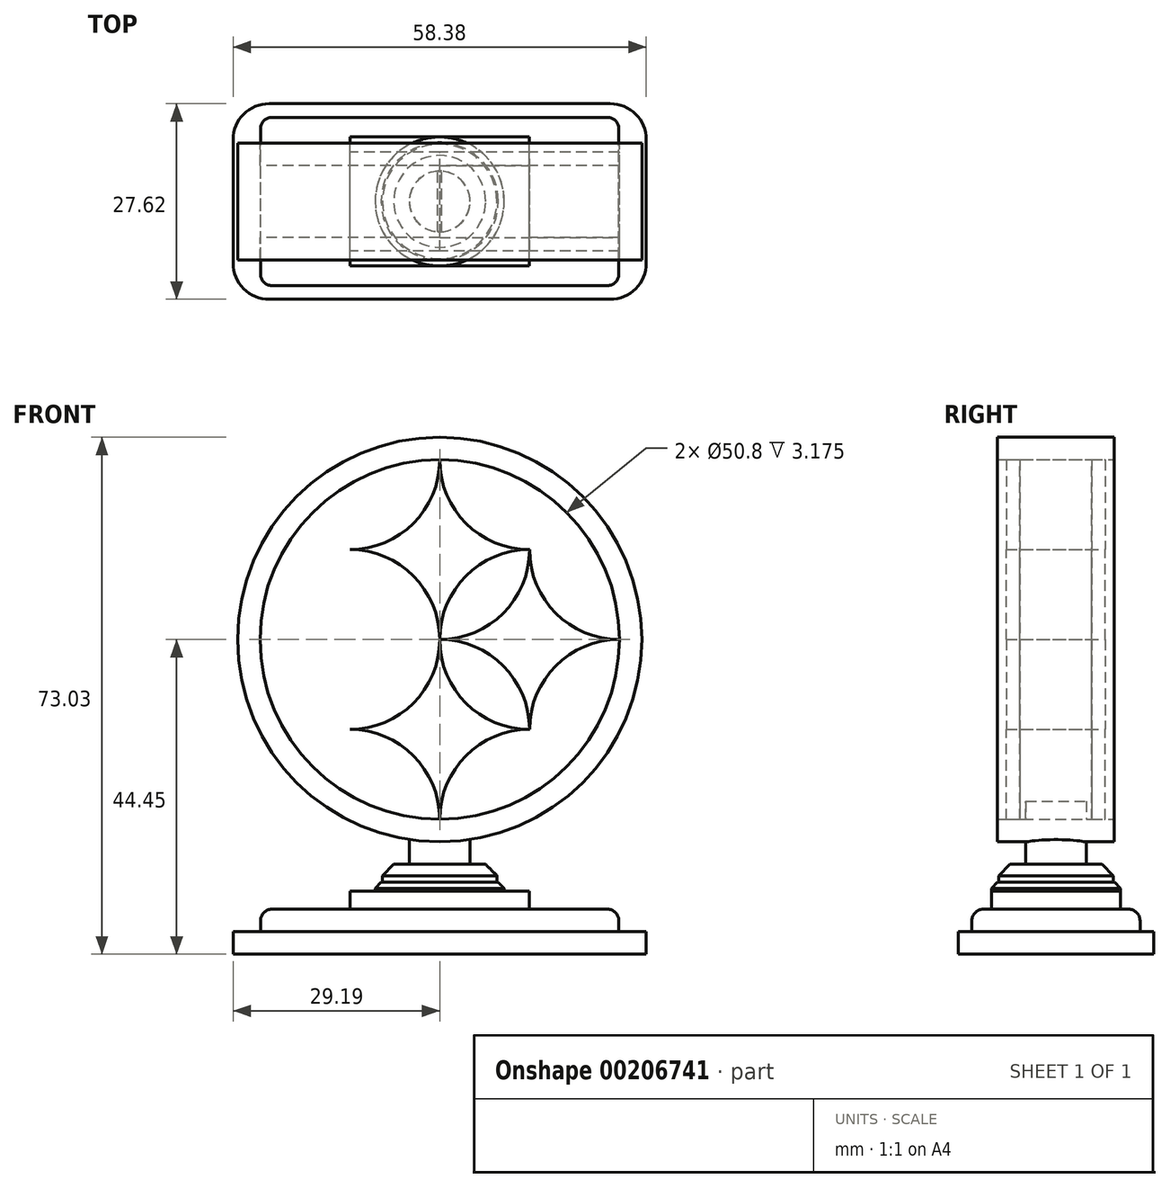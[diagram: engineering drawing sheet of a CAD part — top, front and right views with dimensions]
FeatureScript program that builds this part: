
annotation { "Feature Type Name" : "Feature", "Feature Type Description" : "" }
export const myFeature = defineFeature(function(context is Context, id is Id, definition is map)
    precondition{}
    {
        {
            var Q0;
            Q0=qCreatedBy(makeId("Front.planeOp"),FACE);
            var sketch = newSketch(context, id + "F0", { "sketchPlane" : qUnion([Q0])});
            skCircle(sketch, "E0", {"center": v(0, 44.45) * mm, "radius": 25.4 * mm});
            skCircle(sketch, "E1", {"center": v(0, 44.45) * mm, "radius": 28.58 * mm});
            skArc(sketch, "E2", {"start": v(-12.7, 31.75) * mm, "mid": v(0, 44.45) * mm, "end": v(-12.7, 57.15) * mm});
            skArc(sketch, "E3", {"start": v(12.7, 31.75) * mm, "mid": v(8.98, 40.73) * mm, "end": v(0, 44.45) * mm});
            skArc(sketch, "E4", {"start": v(0, 44.45) * mm, "mid": v(8.98, 48.17) * mm, "end": v(12.7, 57.15) * mm});
            skArc(sketch, "E5", {"start": v(12.7, 57.15) * mm, "mid": v(0, 44.45) * mm, "end": v(12.7, 31.75) * mm});
            skArc(sketch, "E6", {"start": v(0, 69.85) * mm, "mid": v(3.72, 60.87) * mm, "end": v(12.7, 57.15) * mm});
            skArc(sketch, "E7", {"start": v(12.7, 57.15) * mm, "mid": v(16.42, 48.17) * mm, "end": v(25.4, 44.45) * mm});
            skArc(sketch, "E8", {"start": v(25.4, 44.45) * mm, "mid": v(16.42, 40.73) * mm, "end": v(12.7, 31.75) * mm});
            skArc(sketch, "E9.trimOffspring", {"start": v(-12.7, 57.15) * mm, "mid": v(-3.72, 60.87) * mm, "end": v(0, 69.85) * mm});
            skArc(sketch, "E10.trimOffspring", {"start": v(0, 19.05) * mm, "mid": v(-3.72, 28.03) * mm, "end": v(-12.7, 31.75) * mm});
            skArc(sketch, "E11.trimOffspring", {"start": v(12.7, 31.75) * mm, "mid": v(3.72, 28.03) * mm, "end": v(0, 19.05) * mm});
            skSolve(sketch);
        }
        {
            var Q0;
            Q0=qCreatedBy(makeId("Top.planeOp"),FACE);
            var sketch = newSketch(context, id + "F1", { "sketchPlane" : qUnion([Q0])});
            skLineSegment(sketch, "E12.bottom", {"start": v(29.2, -13.81) * mm, "end": v(-29.2, -13.81) * mm});
            skLineSegment(sketch, "E12.top", {"start": v(29.2, 13.81) * mm, "end": v(-29.2, 13.81) * mm});
            skLineSegment(sketch, "E12.left", {"start": v(29.2, -13.81) * mm, "end": v(29.2, 13.81) * mm});
            skLineSegment(sketch, "E12.right", {"start": v(-29.2, -13.81) * mm, "end": v(-29.2, 13.81) * mm});
            skPoint(sketch, "E12.middle", {"position": v(0, 0) * mm});
            skLineSegment(sketch, "E13.bottom", {"start": v(25.33, -11.88) * mm, "end": v(-25.33, -11.88) * mm});
            skLineSegment(sketch, "E13.top", {"start": v(25.33, 11.88) * mm, "end": v(-25.33, 11.88) * mm});
            skLineSegment(sketch, "E13.left", {"start": v(25.33, -11.88) * mm, "end": v(25.33, 11.88) * mm});
            skLineSegment(sketch, "E13.right", {"start": v(-25.33, -11.88) * mm, "end": v(-25.33, 11.88) * mm});
            skLineSegment(sketch, "E14.bottom", {"start": v(12.66, -9.11) * mm, "end": v(-12.66, -9.11) * mm});
            skLineSegment(sketch, "E14.top", {"start": v(12.66, 9.11) * mm, "end": v(-12.66, 9.11) * mm});
            skLineSegment(sketch, "E14.left", {"start": v(12.66, -9.11) * mm, "end": v(12.66, 9.11) * mm});
            skLineSegment(sketch, "E14.right", {"start": v(-12.66, -9.11) * mm, "end": v(-12.66, 9.11) * mm});
            skCircle(sketch, "E15", {"center": v(0, 0) * mm, "radius": 9.11 * mm});
            skCircle(sketch, "E16", {"center": v(0, 0) * mm, "radius": 8.1 * mm});
            skCircle(sketch, "E17", {"center": v(0, 0) * mm, "radius": 4.29 * mm});
            skSolve(sketch);
        }
        {
            var Q0;
            Q0=makeQuery(id+"F1.imprint","IMPRINT",FACE,{"disambiguationData":[TD([[makeQuery(id+"F1.imprint","IMPRINT",EDGE,{"derivedFrom":sQuery(id+"F1.wireOp",EDGE,"E17")}),1.0]])]});
            extrude(context, id + "F2", {"entities" : qUnion([Q0]), "depth" : 21.59 * mm});
        }
        {
            var Q0;
            Q0=makeQuery(id+"F1.imprint","IMPRINT",FACE,{"disambiguationData":[TD([[makeQuery(id+"F1.imprint","IMPRINT",EDGE,{"derivedFrom":sQuery(id+"F1.wireOp",EDGE,"E16")}),1.0]])]});
            extrude(context, id + "F3", {"entities" : qUnion([Q0]), "operationType" : NewBodyOperationType.ADD, "depth" : 12.7 * mm});
        }
        {
            var Q0;
            Q0=makeQuery(id+"F1.imprint","IMPRINT",FACE,{"disambiguationData":[TD([[makeQuery(id+"F1.imprint","IMPRINT",EDGE,{"derivedFrom":sQuery(id+"F1.wireOp",EDGE,"E16")}),-1.0]])]});
            extrude(context, id + "F4", {"entities" : qUnion([Q0]), "operationType" : NewBodyOperationType.ADD, "depth" : 10.16 * mm});
        }
        {
            var Q0;
            {var subQ0=sQuery(id+"F1.wireOp",EDGE,"E14.right");Q0=makeQuery(id+"F1.imprint","IMPRINT",FACE,{"disambiguationData":[TD([[makeQuery(id+"F1.imprint","IMPRINT",EDGE,{"derivedFrom":subQ0}),-1.0]])]});}
            var Q1;
            {var subQ0=sQuery(id+"F1.wireOp",EDGE,"E14.left");Q1=makeQuery(id+"F1.imprint","IMPRINT",FACE,{"disambiguationData":[TD([[makeQuery(id+"F1.imprint","IMPRINT",EDGE,{"derivedFrom":subQ0}),1.0]])]});}
            extrude(context, id + "F5", {"entities" : qUnion([Q0, Q1]), "operationType" : NewBodyOperationType.ADD, "depth" : 8.9 * mm});
        }
        {
            var Q0;
            Q0=makeQuery(id+"F1.imprint","IMPRINT",FACE,{"disambiguationData":[TD([[makeQuery(id+"F1.imprint","IMPRINT",EDGE,{"derivedFrom":sQuery(id+"F1.wireOp",EDGE,"E13.bottom")}),-1.0]])]});
            extrude(context, id + "F6", {"entities" : qUnion([Q0]), "operationType" : NewBodyOperationType.ADD, "depth" : 6.35 * mm});
        }
        {
            var Q0;
            Q0=makeQuery(id+"F1.imprint","IMPRINT",FACE,{"disambiguationData":[TD([[makeQuery(id+"F1.imprint","IMPRINT",EDGE,{"derivedFrom":sQuery(id+"F1.wireOp",EDGE,"E12.bottom")}),-1.0]])]});
            extrude(context, id + "F7", {"entities" : qUnion([Q0]), "operationType" : NewBodyOperationType.ADD, "depth" : 3.17 * mm});
        }
        {
            var Q0;
            Q0=makeQuery(id+"F6.opExtrude","CAP_EDGE",EDGE,{"disambiguationData":[OSD([sQuery(id+"F1.wireOp",EDGE,"E13.bottom")])],"isStart":false});
            fillet(context, id + "F8", {"entities" : qUnion([Q0]), "radius" : 1.6 * mm, "tangentPropagation" : true, "allowEdgeOverflow" : false});
        }
        {
            var Q0;
            Q0=makeQuery(id+"F6.opExtrude","CAP_EDGE",EDGE,{"disambiguationData":[OSD([sQuery(id+"F1.wireOp",EDGE,"E13.right")])],"isStart":false});
            fillet(context, id + "F9", {"entities" : qUnion([Q0]), "radius" : 1.6 * mm, "tangentPropagation" : true, "allowEdgeOverflow" : false});
        }
        {
            var Q0;
            Q0=makeQuery(id+"F6.opExtrude","CAP_EDGE",EDGE,{"disambiguationData":[OSD([sQuery(id+"F1.wireOp",EDGE,"E13.left")])],"isStart":false});
            fillet(context, id + "F10", {"entities" : qUnion([Q0]), "radius" : 1.6 * mm, "tangentPropagation" : true, "allowEdgeOverflow" : false});
        }
        {
            var Q0;
            Q0=makeQuery(id+"F6.opExtrude","CAP_EDGE",EDGE,{"disambiguationData":[OSD([sQuery(id+"F1.wireOp",EDGE,"E13.top")])],"isStart":false});
            fillet(context, id + "F11", {"entities" : qUnion([Q0]), "radius" : 1.6 * mm, "tangentPropagation" : true, "allowEdgeOverflow" : false});
        }
        {
            var Q0;
            Q0=makeQuery(id+"F4.opExtrude","CAP_EDGE",EDGE,{"disambiguationData":[OSD([sQuery(id+"F1.wireOp",EDGE,"E15")])],"isStart":false});
            chamfer(context, id + "F12", {"entities" : qUnion([Q0]), "width" : 0.84 * mm, "tangentPropagation" : true});
        }
        {
            var Q0;
            Q0=makeQuery(id+"F3.opExtrude","CAP_EDGE",EDGE,{"disambiguationData":[OSD([sQuery(id+"F1.wireOp",EDGE,"E16")])],"isStart":false});
            chamfer(context, id + "F13", {"entities" : qUnion([Q0]), "width" : 1.6 * mm, "tangentPropagation" : true});
        }
        {
            var Q0;
            Q0=makeQuery(id+"F7.opExtrude","SWEPT_EDGE",EDGE,{"disambiguationData":[OSD([sQuery(id+"F1.wireOp",EDGE,"E12.bottom"),sQuery(id+"F1.wireOp",EDGE,"E12.left")])]});
            fillet(context, id + "F14", {"entities" : qUnion([Q0]), "radius" : 5.08 * mm, "tangentPropagation" : true, "allowEdgeOverflow" : false});
        }
        {
            var Q0;
            Q0=makeQuery(id+"F7.opExtrude","SWEPT_EDGE",EDGE,{"disambiguationData":[OSD([sQuery(id+"F1.wireOp",EDGE,"E12.bottom"),sQuery(id+"F1.wireOp",EDGE,"E12.right")])]});
            fillet(context, id + "F15", {"entities" : qUnion([Q0]), "radius" : 5.08 * mm, "tangentPropagation" : true, "allowEdgeOverflow" : false});
        }
        {
            var Q0;
            Q0=makeQuery(id+"F7.opExtrude","SWEPT_EDGE",EDGE,{"disambiguationData":[OSD([sQuery(id+"F1.wireOp",EDGE,"E12.top"),sQuery(id+"F1.wireOp",EDGE,"E12.right")])]});
            fillet(context, id + "F16", {"entities" : qUnion([Q0]), "radius" : 5.08 * mm, "tangentPropagation" : true, "allowEdgeOverflow" : false});
        }
        {
            var Q0;
            Q0=makeQuery(id+"F7.opExtrude","SWEPT_EDGE",EDGE,{"disambiguationData":[OSD([sQuery(id+"F1.wireOp",EDGE,"E12.top"),sQuery(id+"F1.wireOp",EDGE,"E12.left")])]});
            fillet(context, id + "F17", {"entities" : qUnion([Q0]), "radius" : 5.08 * mm, "tangentPropagation" : true, "allowEdgeOverflow" : false});
        }
        {
            var Q0;
            Q0=makeQuery(id+"F0.imprint","IMPRINT",FACE,{"disambiguationData":[TD([[makeQuery(id+"F0.imprint","IMPRINT",EDGE,{"derivedFrom":sQuery(id+"F0.wireOp",EDGE,"E1")}),1.0]])]});
            extrude(context, id + "F18", {"entities" : qUnion([Q0]), "operationType" : NewBodyOperationType.ADD, "endBound" : BoundingType.SYMMETRIC, "depth" : 16.5 * mm});
        }
        {
            var Q0;
            {var subQ0=sQuery(id+"F0.wireOp",EDGE,"E9.trimOffspring");Q0=makeQuery(id+"F0.imprint","IMPRINT",FACE,{"disambiguationData":[TD([[makeQuery(id+"F0.imprint","IMPRINT",EDGE,{"derivedFrom":subQ0}),1.0]])]});}
            var Q1;
            {var subQ0=sQuery(id+"F0.wireOp",EDGE,"E4");Q1=makeQuery(id+"F0.imprint","IMPRINT",FACE,{"disambiguationData":[TD([[makeQuery(id+"F0.imprint","IMPRINT",EDGE,{"derivedFrom":subQ0}),1.0]])]});}
            var Q2;
            {var subQ0=sQuery(id+"F0.wireOp",EDGE,"E3");Q2=makeQuery(id+"F0.imprint","IMPRINT",FACE,{"disambiguationData":[TD([[makeQuery(id+"F0.imprint","IMPRINT",EDGE,{"derivedFrom":subQ0}),1.0]])]});}
            var Q3;
            {var subQ0=sQuery(id+"F0.wireOp",EDGE,"E8");Q3=makeQuery(id+"F0.imprint","IMPRINT",FACE,{"disambiguationData":[TD([[makeQuery(id+"F0.imprint","IMPRINT",EDGE,{"derivedFrom":subQ0}),1.0]])]});}
            var Q4;
            {var subQ0=sQuery(id+"F0.wireOp",EDGE,"E6");Q4=makeQuery(id+"F0.imprint","IMPRINT",FACE,{"disambiguationData":[TD([[makeQuery(id+"F0.imprint","IMPRINT",EDGE,{"derivedFrom":subQ0}),1.0]])]});}
            extrude(context, id + "F19", {"entities" : qUnion([Q0, Q1, Q2, Q3, Q4]), "operationType" : NewBodyOperationType.ADD, "endBound" : BoundingType.SYMMETRIC, "depth" : 10.16 * mm});
        }
        {
            var Q0;
            {var subQ5=sQuery(id+"F0.wireOp",EDGE,"E6");Q0=makeQuery(id+"F0.imprint","IMPRINT",FACE,{"disambiguationData":[TD([[makeQuery(id+"F0.imprint","IMPRINT",EDGE,{"derivedFrom":subQ5}),-1.0]])]});}
            var Q1;
            Q1=makeQuery(id+"F0.imprint","IMPRINT",FACE,{"disambiguationData":[TD([[makeQuery(id+"F0.imprint","IMPRINT",EDGE,{"derivedFrom":sQuery(id+"F0.wireOp",EDGE,"E3")}),-1.0]])]});
            var Q2;
            {var subQ0=sQuery(id+"F0.wireOp",EDGE,"E10.trimOffspring");Q2=makeQuery(id+"F0.imprint","IMPRINT",FACE,{"disambiguationData":[TD([[makeQuery(id+"F0.imprint","IMPRINT",EDGE,{"derivedFrom":subQ0}),-1.0]])]});}
            extrude(context, id + "F20", {"entities" : qUnion([Q0, Q1, Q2]), "endBound" : BoundingType.SYMMETRIC, "depth" : 13.97 * mm});
        }
    });
